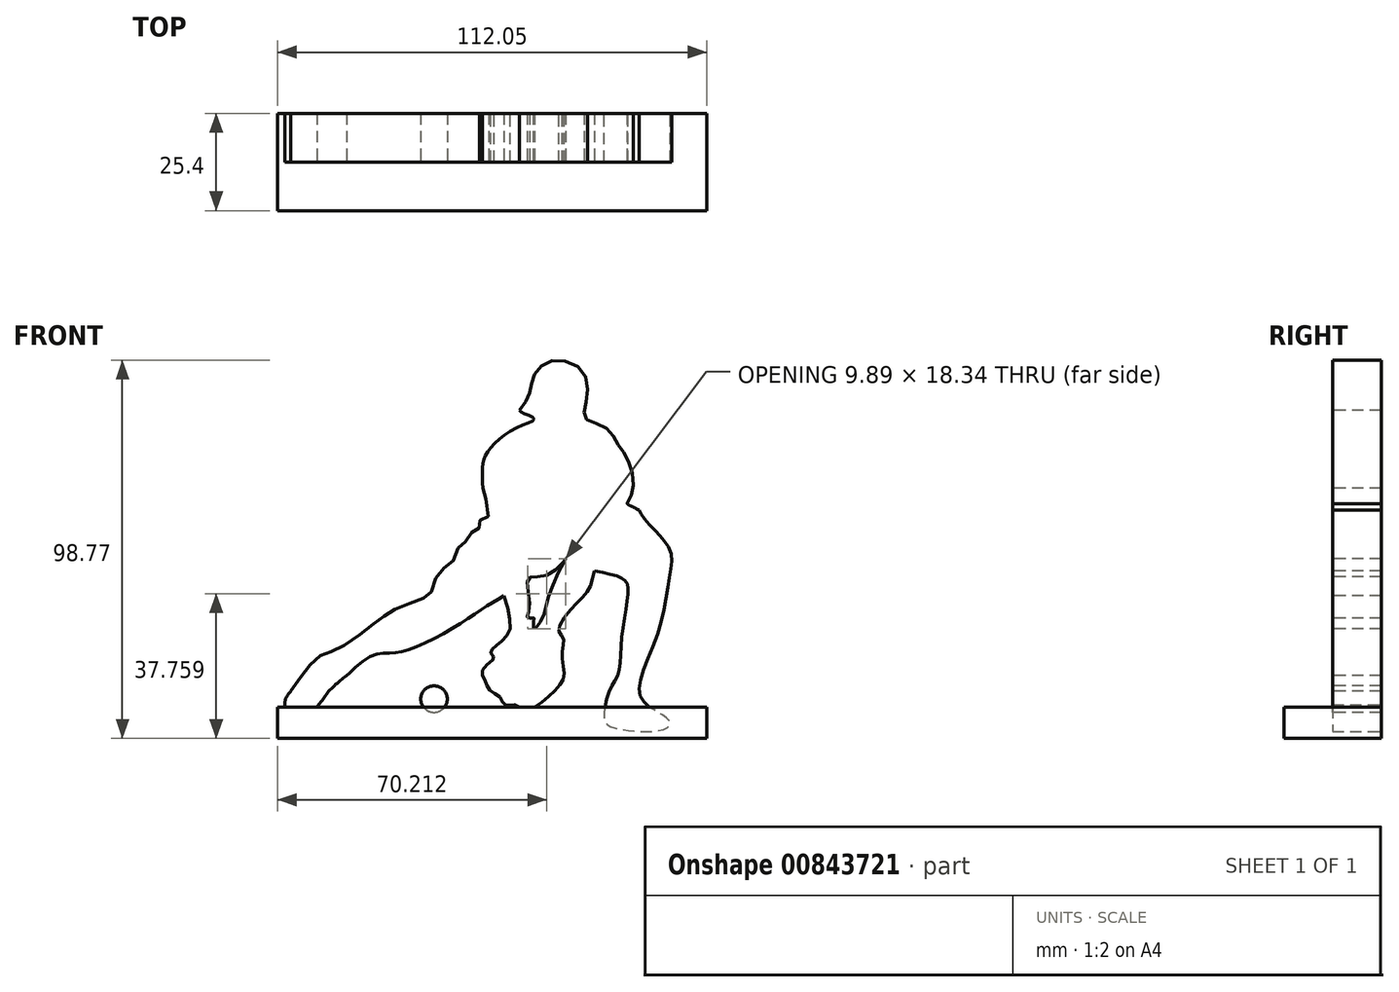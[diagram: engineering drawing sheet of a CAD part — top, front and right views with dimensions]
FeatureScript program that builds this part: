
annotation { "Feature Type Name" : "Feature", "Feature Type Description" : "" }
export const myFeature = defineFeature(function(context is Context, id is Id, definition is map)
    precondition{}
    {
        {
            var Q0;
            Q0=qCreatedBy(makeId("Front.planeOp"),FACE);
            var sketch = newSketch(context, id + "F0", { "sketchPlane" : qUnion([Q0])});
            skFitSpline(sketch, "E0", {"points": [v(-54.6, -33.47) * mm, v(-50.08, -27.24) * mm, v(-46.23, -23.79) * mm, v(-42.65, -22.6) * mm, v(-35.09, -17.55) * mm, v(-30.44, -13.97) * mm, v(-26.46, -11.7) * mm, v(-20.09, -9.19) * mm, v(-17.97, -7.6) * mm, v(-15.84, -2.29) * mm, v(-12.53, 0) * mm, v(-10.67, 4.35) * mm, v(-8.68, 5.94) * mm, v(-6.82, 8.6) * mm, v(-5.36, 9.26) * mm, v(-5.1, 11.25) * mm, v(-3.1, 12.18) * mm, v(-4.49, 19.27) * mm, v(-4.49, 19.5) * mm], "startDerivative": vector(57.94, 85.5) * mm, "endDerivative": vector(4.03, 7.76) * mm});
            skFitSpline(sketch, "E1", {"points": [v(-4.49, 19.5) * mm, v(-4.49, 25.51) * mm, v(-2.97, 29.42) * mm, v(4.4, 35.33) * mm, v(8.86, 37.68) * mm, v(5.62, 39.35) * mm, v(5.07, 40.13) * mm], "startDerivative": vector(-1.57, 33.4) * mm, "endDerivative": vector(-2.6, 9.92) * mm});
            skFitSpline(sketch, "E2", {"points": [v(17.14, 1.14) * mm, v(13.29, -6.96) * mm, v(11.03, -14.52) * mm, v(8.86, -17.18) * mm, v(8.86, -14.79) * mm, v(8.86, -14.39) * mm, v(7.18, -14.26) * mm, v(7.71, -12) * mm, v(7.45, -4.04) * mm, v(12.62, -3.1) * mm, v(17.14, 1.14) * mm]});
            skFitSpline(sketch, "E3", {"points": [v(1.08, -8.55) * mm, v(-3.96, -11.6) * mm, v(-11.26, -16.38) * mm, v(-22.94, -22.35) * mm, v(-28.65, -23.55) * mm, v(-34.22, -24.6) * mm, v(-40.06, -29.38) * mm, v(-40.2, -29.38) * mm], "startDerivative": vector(-34.53, -20.13) * mm, "endDerivative": vector(-4.25, 2.37) * mm});
            skFitSpline(sketch, "E4", {"points": [v(-40.06, -29.38) * mm, v(-44.75, -33.61) * mm, v(-47.94, -37.73) * mm, v(-51.23, -39.59) * mm, v(-54.89, -39.32) * mm, v(-56.08, -36.14) * mm, v(-54.6, -33.47) * mm], "startDerivative": vector(-24.66, -19.52) * mm, "endDerivative": vector(14.14, 16.89) * mm});
            skFitSpline(sketch, "E5", {"points": [v(1.08, -8.55) * mm, v(2.54, -17.55) * mm, v(0, -20.74) * mm, v(-2.06, -22.6) * mm, v(-2.25, -23.79) * mm, v(-1.5, -24.72) * mm, v(-4.12, -27.24) * mm, v(-4.5, -29.38) * mm, v(-3.65, -31.28) * mm, v(-2.43, -33.47) * mm, v(0, -34.94) * mm, v(1.08, -36.93) * mm, v(2.91, -37.06) * mm, v(3.95, -37.06) * mm, v(7.45, -38) * mm, v(13.99, -33.61) * mm, v(16.7, -29.38) * mm, v(16.24, -23.79) * mm, v(16.52, -19.68) * mm, v(15.4, -17.55) * mm, v(19.71, -10.79) * mm, v(23.56, -6.15) * mm, v(24.59, -2.16) * mm, v(24.68, -2.03) * mm], "startDerivative": vector(42.23, -140.23) * mm, "endDerivative": vector(9.4, 7.13) * mm});
            skFitSpline(sketch, "E6", {"points": [v(36.32, 13.82) * mm, v(33.2, 15.49) * mm, v(33.2, 15.6) * mm], "startDerivative": vector(-5.24, 2.5) * mm, "endDerivative": vector(0.28, 0.65) * mm});
            skFitSpline(sketch, "E7", {"points": [v(5.13, 39.88) * mm, v(7.8, 44.47) * mm, v(8.81, 48.82) * mm, v(13.6, 52.84) * mm, v(21.64, 49.94) * mm, v(22.54, 42.01) * mm, v(22.31, 37.77) * mm, v(27.56, 35.33) * mm, v(30.68, 31.2) * mm, v(33.2, 27.17) * mm, v(34.81, 20.03) * mm, v(33.2, 15.49) * mm], "startDerivative": vector(37.7, 52.38) * mm, "endDerivative": vector(-26.93, -49.48) * mm});
            skFitSpline(sketch, "E8", {"points": [v(24.68, -2.03) * mm, v(31.48, -3.8) * mm, v(33.2, -5.37) * mm, v(33.2, -9.79) * mm, v(31.64, -21) * mm, v(30.85, -28.88) * mm, v(28.49, -33.46) * mm, v(27.22, -40.56) * mm, v(29.12, -42.77) * mm, v(42.85, -43.4) * mm, v(44.29, -41.35) * mm, v(39.06, -37.56) * mm, v(36.32, -32.67) * mm, v(41.27, -18.15) * mm, v(44.29, -3.48) * mm, v(44.29, 3.57) * mm, v(38.11, 11.04) * mm, v(36.32, 13.82) * mm], "startDerivative": vector(132.73, -26.81) * mm, "endDerivative": vector(-30.24, 60.34) * mm});
            skCircle(sketch, "E9", {"center": v(-17.2, -35.53) * mm, "radius": 3.45 * mm});
            skLineSegment(sketch, "E10.bottom", {"start": v(-74.96, -37.56) * mm, "end": v(61.7, -37.56) * mm});
            skLineSegment(sketch, "E10.top", {"start": v(-74.96, -48.92) * mm, "end": v(61.7, -48.92) * mm});
            skLineSegment(sketch, "E10.left", {"start": v(-74.96, -37.56) * mm, "end": v(-74.96, -48.92) * mm});
            skLineSegment(sketch, "E10.right", {"start": v(61.7, -37.56) * mm, "end": v(61.7, -48.92) * mm});
            skSolve(sketch);
        }
        {
            var Q0;
            Q0=makeQuery(id+"F0.imprint","IMPRINT",FACE,{"disambiguationData":[TD([[makeQuery(id+"F0.imprint","IMPRINT",EDGE,{"derivedFrom":sQuery(id+"F0.wireOp",EDGE,"E9")}),1.0]])]});
            var Q1;
            {var subQ4=sQuery(id+"F0.wireOp",EDGE,"E0");Q1=makeQuery(id+"F0.imprint","IMPRINT",FACE,{"disambiguationData":[TD([[makeQuery(id+"F0.imprint","IMPRINT",EDGE,{"derivedFrom":subQ4}),-1.0]])]});}
            var Q2;
            {var subQ0=sQuery(id+"F0.wireOp",EDGE,"E10.bottom");var subQ1=sQuery(id+"F0.wireOp",EDGE,"E4");var subQ2=makeQuery(id+"F0.imprint","INTERSECT",VERTEX,{"disambiguationData":[OD(0.0)],"derivedFrom":[subQ1,subQ0]});Q2=makeQuery(id+"F0.imprint","IMPRINT",FACE,{"disambiguationData":[TD([[makeQuery(id+"F0.imprint","IMPRINT",EDGE,{"disambiguationData":[TD([[subQ2,1.0]])],"derivedFrom":subQ1}),-1.0]])]});}
            var Q3;
            {var subQ0=sQuery(id+"F0.wireOp",EDGE,"E10.bottom");var subQ1=sQuery(id+"F0.wireOp",EDGE,"E8");var subQ2=makeQuery(id+"F0.imprint","INTERSECT",VERTEX,{"disambiguationData":[OD(0.0)],"derivedFrom":[subQ1,subQ0]});Q3=makeQuery(id+"F0.imprint","IMPRINT",FACE,{"disambiguationData":[TD([[makeQuery(id+"F0.imprint","IMPRINT",EDGE,{"disambiguationData":[TD([[subQ2,1.0]])],"derivedFrom":subQ1}),1.0]])]});}
            extrude(context, id + "F1", {"entities" : qUnion([Q0, Q1, Q2, Q3]), "oppositeDirection" : true, "depth" : 12.7 * mm, "offsetDistance" : 25.4 * mm});
        }
        {
            var Q0;
            Q0=qCreatedBy(makeId("Front.planeOp"),FACE);
            var sketch = newSketch(context, id + "F2", { "sketchPlane" : qUnion([Q0])});
            skLineSegment(sketch, "E11.bottom", {"start": v(-58.02, -37.59) * mm, "end": v(54.03, -37.59) * mm});
            skLineSegment(sketch, "E11.top", {"start": v(-58.02, -45.8) * mm, "end": v(54.03, -45.8) * mm});
            skLineSegment(sketch, "E11.left", {"start": v(-58.02, -37.59) * mm, "end": v(-58.02, -45.8) * mm});
            skLineSegment(sketch, "E11.right", {"start": v(54.03, -37.59) * mm, "end": v(54.03, -45.8) * mm});
            skSolve(sketch);
        }
        {
            var Q0;
            Q0 = qSketchRegion(id + "F2", true);
            extrude(context, id + "F3", {"entities" : qUnion([Q0]), "endBound" : BoundingType.SYMMETRIC, "depth" : 25.4 * mm, "offsetDistance" : 25.4 * mm});
        }
    });
